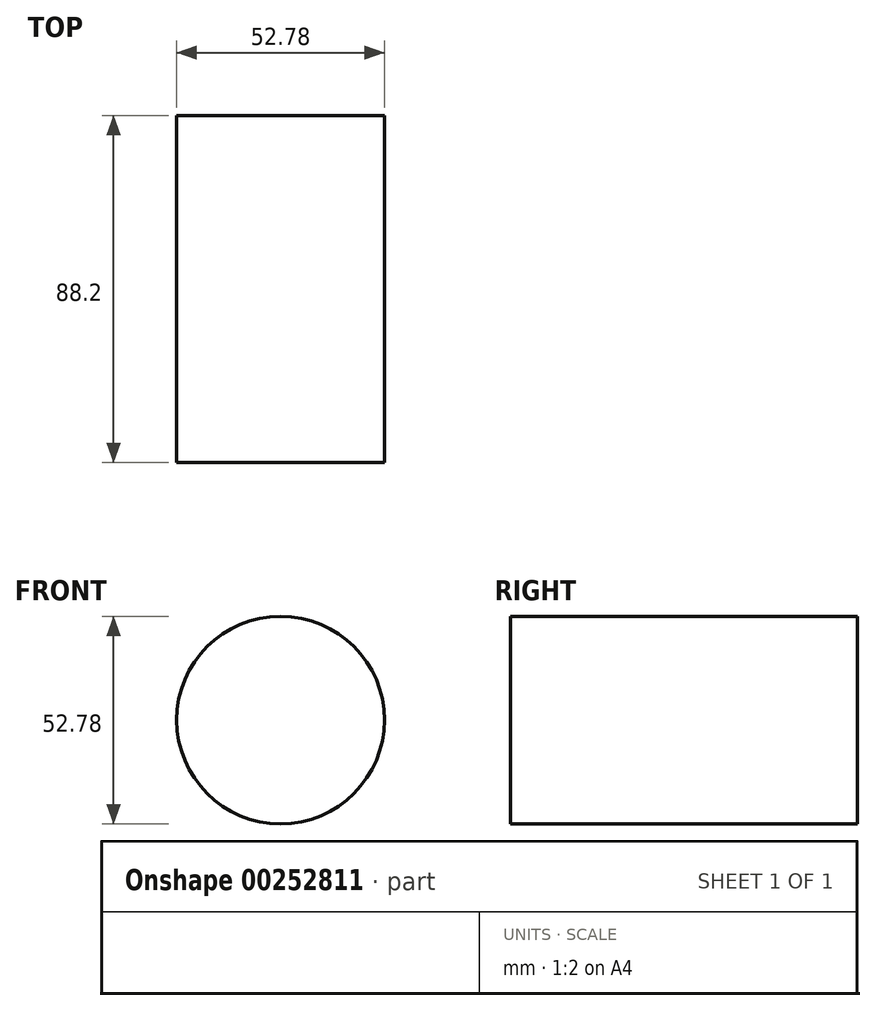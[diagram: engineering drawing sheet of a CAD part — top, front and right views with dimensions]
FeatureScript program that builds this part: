
annotation { "Feature Type Name" : "Feature", "Feature Type Description" : "" }
export const myFeature = defineFeature(function(context is Context, id is Id, definition is map)
    precondition{}
    {
        {
            var Q0;
            Q0=qCreatedBy(makeId("Top.planeOp"),FACE);
            var sketch = newSketch(context, id + "F0", { "sketchPlane" : qUnion([Q0])});
            skLineSegment(sketch, "E0.bottom", {"start": v(-26.4, 50.35) * mm, "end": v(26.4, 50.35) * mm});
            skLineSegment(sketch, "E0.top", {"start": v(-26.4, -50.35) * mm, "end": v(26.4, -50.35) * mm});
            skLineSegment(sketch, "E0.left", {"start": v(-26.4, 50.35) * mm, "end": v(-26.4, -50.35) * mm});
            skLineSegment(sketch, "E0.right", {"start": v(26.4, 50.35) * mm, "end": v(26.4, -50.35) * mm});
            skPoint(sketch, "E0.middle", {"position": v(0, 0) * mm});
            skLineSegment(sketch, "E1", {"start": v(0, 50.35) * mm, "end": v(0, -50.35) * mm});
            skLineSegment(sketch, "E2", {"start": v(0, -50.35) * mm, "end": v(0, 50.35) * mm});
            skSolve(sketch);
        }
        {
            var Q0;
            {var subQ0=sQuery(id+"F0.wireOp",EDGE,"E0.left");Q0=makeQuery(id+"F0.imprint","IMPRINT",FACE,{"disambiguationData":[TD([[makeQuery(id+"F0.imprint","IMPRINT",EDGE,{"derivedFrom":subQ0}),1.0]])]});}
            var Q1;
            Q1=sQuery(id+"F0.wireOp",EDGE,"E2");
            revolve(context, id + "F1", {"entities" : qUnion([Q0]), "axis" : qUnion([Q1]), "revolveType" : RevolveType.FULL});
        }
        {
            var Q0;
            Q0=makeQuery(id+"F1.opRevolve","SWEPT_FACE",FACE,{"disambiguationData":[OSD([sQuery(id+"F0.wireOp",EDGE,"E0.bottom")])]});
            extrude(context, id + "F2", {"entities" : qUnion([Q0]), "operationType" : NewBodyOperationType.REMOVE, "endBound" : BoundingType.SYMMETRIC, "oppositeDirection" : true, "depth" : 25 * mm});
        }
    });
